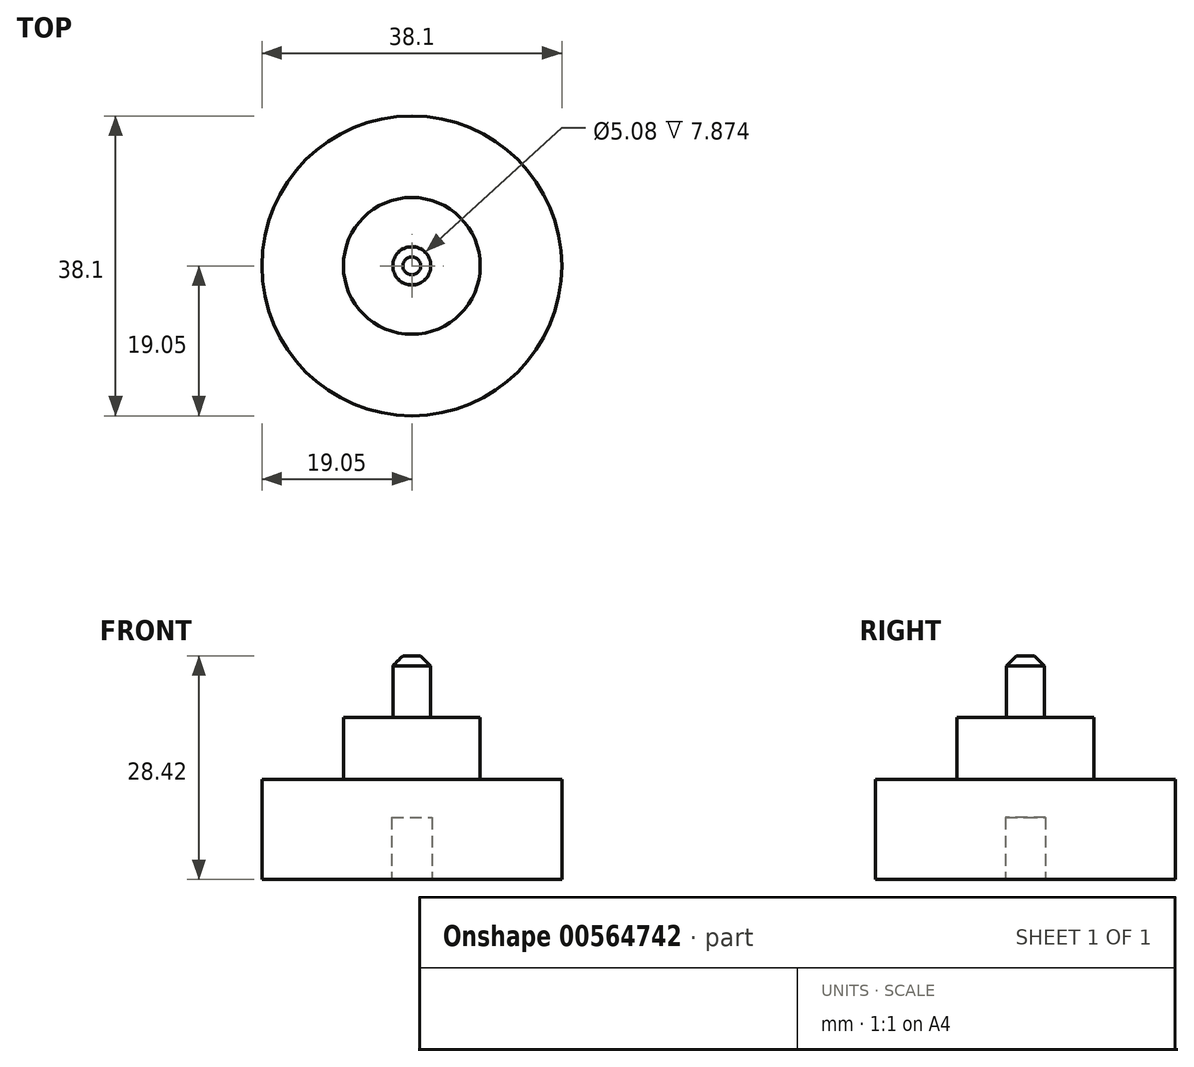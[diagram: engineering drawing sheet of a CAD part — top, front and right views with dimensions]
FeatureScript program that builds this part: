
annotation { "Feature Type Name" : "Feature", "Feature Type Description" : "" }
export const myFeature = defineFeature(function(context is Context, id is Id, definition is map)
    precondition{}
    {
        {
            var Q0;
            Q0=qCreatedBy(makeId("Front.planeOp"),FACE);
            var sketch = newSketch(context, id + "F0", { "sketchPlane" : qUnion([Q0])});
            skLineSegment(sketch, "E0", {"start": v(19.05, 0) * mm, "end": v(19.05, 12.7) * mm});
            skLineSegment(sketch, "E1", {"start": v(19.05, 12.7) * mm, "end": v(8.69, 12.7) * mm});
            skLineSegment(sketch, "E2", {"start": v(2.4, 20.57) * mm, "end": v(8.69, 20.57) * mm});
            skLineSegment(sketch, "E3", {"start": v(8.69, 20.57) * mm, "end": v(8.69, 12.7) * mm});
            skLineSegment(sketch, "E4", {"start": v(0, 28.42) * mm, "end": v(2.4, 28.42) * mm});
            skLineSegment(sketch, "E5", {"start": v(2.4, 28.42) * mm, "end": v(2.4, 20.57) * mm});
            skPoint(sketch, "E5.endSnap0", {"position": v(4.34, 20.57) * mm});
            skLineSegment(sketch, "E6", {"start": v(2.54, 0) * mm, "end": v(2.54, 7.87) * mm});
            skLineSegment(sketch, "E7", {"start": v(2.54, 7.87) * mm, "end": v(0, 7.87) * mm});
            skLineSegment(sketch, "E8", {"start": v(2.54, 0) * mm, "end": v(19.05, 0) * mm});
            skLineSegment(sketch, "E9", {"start": v(0, 7.87) * mm, "end": v(0, 28.42) * mm});
            skSolve(sketch);
        }
        {
            var Q0;
            Q0 = qSketchRegion(id + "F0", true);
            var Q1;
            Q1=sQuery(id+"F0.wireOp",EDGE,"E9");
            revolve(context, id + "F1", {"entities" : qUnion([Q0]), "axis" : qUnion([Q1]), "revolveType" : RevolveType.FULL});
        }
        {
            var Q0;
            Q0=makeQuery(id+"F1.opRevolve","SWEPT_EDGE",EDGE,{"disambiguationData":[OSD([sQuery(id+"F0.wireOp",EDGE,"E4"),sQuery(id+"F0.wireOp",EDGE,"E5")])]});
            chamfer(context, id + "F2", {"entities" : qUnion([Q0]), "width" : 1.27 * mm, "tangentPropagation" : true});
        }
    });
